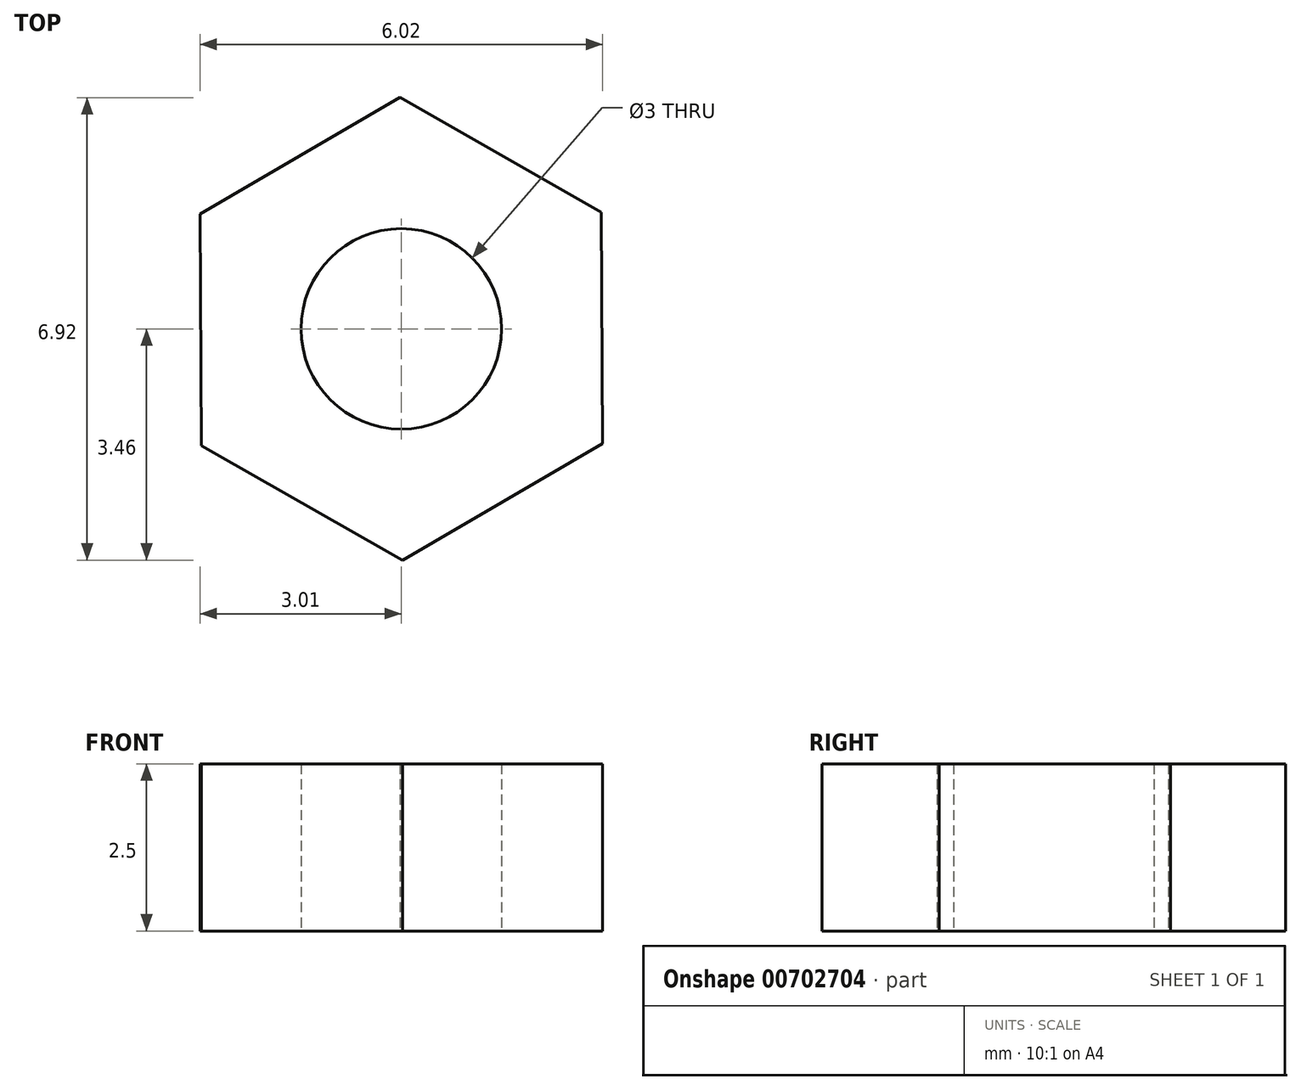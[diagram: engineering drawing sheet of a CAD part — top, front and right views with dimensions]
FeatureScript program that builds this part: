
annotation { "Feature Type Name" : "Feature", "Feature Type Description" : "" }
export const myFeature = defineFeature(function(context is Context, id is Id, definition is map)
    precondition{}
    {
        {
            var Q0;
            Q0=qCreatedBy(makeId("Top.planeOp"),FACE);
            var sketch = newSketch(context, id + "F0", { "sketchPlane" : qUnion([Q0])});
            skCircle(sketch, "E0.cCircle", {"center": v(0, 0) * mm, "radius": 3 * mm, "construction": true});
            skLineSegment(sketch, "E0.0", {"start": v(-3, 1.72) * mm, "end": v(-0.02, 3.46) * mm});
            skLineSegment(sketch, "E0.1", {"start": v(-0.02, 3.46) * mm, "end": v(3, 1.75) * mm});
            skLineSegment(sketch, "E0.2", {"start": v(3, 1.75) * mm, "end": v(3, -1.72) * mm});
            skLineSegment(sketch, "E0.3", {"start": v(3, -1.72) * mm, "end": v(0.02, -3.46) * mm});
            skLineSegment(sketch, "E0.4", {"start": v(0.02, -3.46) * mm, "end": v(-3, -1.75) * mm});
            skLineSegment(sketch, "E0.5", {"start": v(-3, -1.75) * mm, "end": v(-3, 1.72) * mm});
            skPoint(sketch, "E0.0.midPoint", {"position": v(-1.51, 2.6) * mm});
            skCircle(sketch, "E1", {"center": v(0, 0) * mm, "radius": 1.5 * mm});
            skSolve(sketch);
        }
        {
            var Q0;
            Q0=makeQuery(id+"F0.imprint","IMPRINT",FACE,{"disambiguationData":[TD([[makeQuery(id+"F0.imprint","IMPRINT",EDGE,{"derivedFrom":sQuery(id+"F0.wireOp",EDGE,"E0.0")}),-1.0]])]});
            extrude(context, id + "F1", {"entities" : qUnion([Q0]), "depth" : 2.5 * mm, "offsetDistance" : 25.4 * mm});
        }
    });
